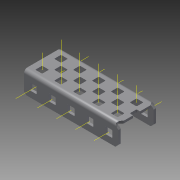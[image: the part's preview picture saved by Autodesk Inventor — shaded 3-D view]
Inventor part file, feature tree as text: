
AUTODESK INVENTOR PART (.ipt)
format: ipt  version: 2015 (Build 190159000, 159)  size: 1,874,432 bytes
history: native  units: in
note: dims shown in document units (in); Inventor stores cm internally (conversion verified against a paired STEP export)
features: other x31, pattern_linear x3, sheet_metal_op x1, extrude x1, imported_body x1, sketch x1
ambient origin geometry x8: Origin, YZ Plane, XZ Plane, XY Plane, X Axis, Y Axis, Z Axis, Center Point
bodies: Body1 (feature_tree)
feature tree (38):
  sheet_metal_op  "Fold1"
  other  "C-Channel"
  extrude  "length cut"  Depth=0.5in
  other  "top axis"
  other  "inner axis"
  other  "front axis"
  other  "back axis"
  pattern_linear  "top axes"  Spacing1=0.5in  [1 undecoded]
  pattern_linear  "inner axes"  Spacing1=0.5in  [1 undecoded]
  pattern_linear  "horiz axes"  Spacing1=-2.5in  [1 undecoded]
  other  "right plane"
  imported_body  "Base1"
  sketch  "Sketch1"  dims[d1=0.0in d4=0.5in d5=0.7874in d7=0.5in d10=0.5in d13=0.5in d14=-2.5in d15=0.0in d16=0.0in d17=0.0in d18=0.0in d19=0.0in]
  other  "Work Point1"
  other  "Work Point2"
  other  "Work Point3"
  other  "Work Point4"
  other  "Work Axis5"
  other  "Work Axis6"
  other  "Work Axis7"
  other  "Work Axis8"
  other  "Work Axis11"
  other  "Work Axis12"
  other  "Work Axis13"
  other  "Work Axis14"
  other  "Work Axis15"
  other  "Work Axis18"
  other  "Work Axis19"
  other  "Work Axis20"
  other  "Work Axis23"
  other  "Work Axis24"
  other  "Work Axis25"
  other  "Work Axis26"
  other  "Work Axis30"
  other  "Work Axis31"
  other  "Work Axis32"
  other  "Work Axis33"
  other  "left plane"
note: 3 required parameter values undecoded (feature->parameter linkage not recoverable at this tier; creation-order binding heuristic only, values carry confidence <= 0.55)
